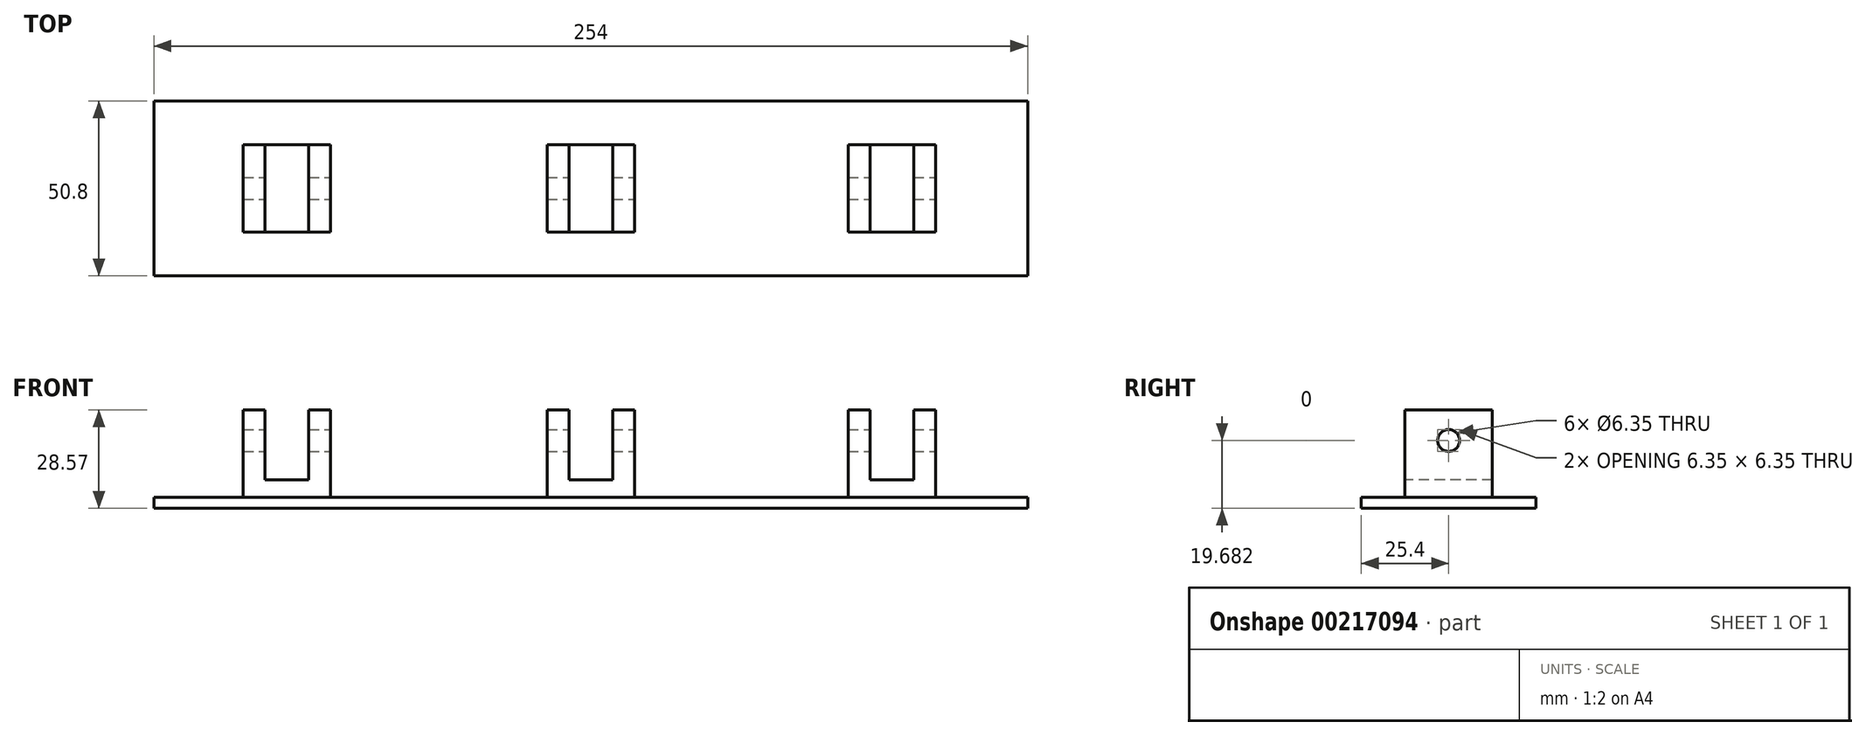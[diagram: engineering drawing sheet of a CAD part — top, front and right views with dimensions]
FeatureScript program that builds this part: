
annotation { "Feature Type Name" : "Feature", "Feature Type Description" : "" }
export const myFeature = defineFeature(function(context is Context, id is Id, definition is map)
    precondition{}
    {
        {
            var Q0;
            Q0=qCreatedBy(makeId("Top.planeOp"),FACE);
            var sketch = newSketch(context, id + "F0", { "sketchPlane" : qUnion([Q0])});
            skLineSegment(sketch, "E0.bottom", {"start": v(127, -25.4) * mm, "end": v(-127, -25.4) * mm});
            skLineSegment(sketch, "E0.top", {"start": v(127, 25.4) * mm, "end": v(-127, 25.4) * mm});
            skLineSegment(sketch, "E0.left", {"start": v(127, -25.4) * mm, "end": v(127, 25.4) * mm});
            skLineSegment(sketch, "E0.right", {"start": v(-127, -25.4) * mm, "end": v(-127, 25.4) * mm});
            skPoint(sketch, "E0.middle", {"position": v(0, 0) * mm});
            skSolve(sketch);
        }
        {
            var Q0;
            Q0=makeQuery(id+"F0.imprint","IMPRINT",FACE,{"disambiguationData":[TD([[makeQuery(id+"F0.imprint","IMPRINT",EDGE,{"derivedFrom":sQuery(id+"F0.wireOp",EDGE,"E0.bottom")}),-1.0]])]});
            extrude(context, id + "F1", {"entities" : qUnion([Q0]), "depth" : 3.17 * mm});
        }
        {
            var Q0;
            Q0=makeQuery(id+"F1.opExtrude","CAP_FACE",FACE,{"disambiguationData":[OSD([sQuery(id+"F0.wireOp",EDGE,"E0.bottom"),sQuery(id+"F0.wireOp",EDGE,"E0.top"),sQuery(id+"F0.wireOp",EDGE,"E0.left"),sQuery(id+"F0.wireOp",EDGE,"E0.right")])],"isStart":false});
            var sketch = newSketch(context, id + "F2", { "sketchPlane" : qUnion([Q0])});
            skLineSegment(sketch, "E1.bottom", {"start": v(12.7, -12.7) * mm, "end": v(-12.7, -12.7) * mm});
            skLineSegment(sketch, "E1.top", {"start": v(12.7, 12.7) * mm, "end": v(-12.7, 12.7) * mm});
            skLineSegment(sketch, "E1.left", {"start": v(12.7, -12.7) * mm, "end": v(12.7, 12.7) * mm});
            skLineSegment(sketch, "E1.right", {"start": v(-12.7, -12.7) * mm, "end": v(-12.7, 12.7) * mm});
            skPoint(sketch, "E1.middle", {"position": v(0, 0) * mm});
            skLineSegment(sketch, "E2.bottom", {"start": v(-75.67, -12.7) * mm, "end": v(-101.07, -12.7) * mm});
            skLineSegment(sketch, "E2.top", {"start": v(-75.67, 12.7) * mm, "end": v(-101.07, 12.7) * mm});
            skLineSegment(sketch, "E2.left", {"start": v(-75.67, -12.7) * mm, "end": v(-75.67, 12.7) * mm});
            skLineSegment(sketch, "E2.right", {"start": v(-101.07, -12.7) * mm, "end": v(-101.07, 12.7) * mm});
            skPoint(sketch, "E2.middle", {"position": v(-88.37, 0) * mm});
            skLineSegment(sketch, "E3.bottom", {"start": v(100.19, -12.7) * mm, "end": v(74.79, -12.7) * mm});
            skLineSegment(sketch, "E3.top", {"start": v(100.19, 12.7) * mm, "end": v(74.79, 12.7) * mm});
            skLineSegment(sketch, "E3.left", {"start": v(100.19, -12.7) * mm, "end": v(100.19, 12.7) * mm});
            skLineSegment(sketch, "E3.right", {"start": v(74.79, -12.7) * mm, "end": v(74.79, 12.7) * mm});
            skPoint(sketch, "E3.middle", {"position": v(87.49, 0) * mm});
            skSolve(sketch);
        }
        {
            var Q0;
            Q0=makeQuery(id+"F2.imprint","IMPRINT",FACE,{"disambiguationData":[TD([[makeQuery(id+"F2.imprint","IMPRINT",EDGE,{"derivedFrom":sQuery(id+"F2.wireOp",EDGE,"E2.bottom")}),-1.0]])]});
            var Q1;
            Q1=makeQuery(id+"F2.imprint","IMPRINT",FACE,{"disambiguationData":[TD([[makeQuery(id+"F2.imprint","IMPRINT",EDGE,{"derivedFrom":sQuery(id+"F2.wireOp",EDGE,"E1.bottom")}),-1.0]])]});
            var Q2;
            Q2=makeQuery(id+"F2.imprint","IMPRINT",FACE,{"disambiguationData":[TD([[makeQuery(id+"F2.imprint","IMPRINT",EDGE,{"derivedFrom":sQuery(id+"F2.wireOp",EDGE,"E3.bottom")}),-1.0]])]});
            extrude(context, id + "F3", {"entities" : qUnion([Q0, Q1, Q2]), "operationType" : NewBodyOperationType.ADD, "depth" : 25.4 * mm});
        }
        {
            var Q0;
            Q0=makeQuery(id+"F3.opExtrude","SWEPT_FACE",FACE,{"disambiguationData":[OSD([sQuery(id+"F2.wireOp",EDGE,"E2.bottom")])]});
            var sketch = newSketch(context, id + "F4", { "sketchPlane" : qUnion([Q0])});
            skLineSegment(sketch, "E4.bottom", {"start": v(-82.02, 8.2) * mm, "end": v(-94.72, 8.2) * mm});
            skLineSegment(sketch, "E4.top", {"start": v(-82.02, 48.95) * mm, "end": v(-94.72, 48.95) * mm});
            skLineSegment(sketch, "E4.left", {"start": v(-82.02, 8.2) * mm, "end": v(-82.02, 48.95) * mm});
            skLineSegment(sketch, "E4.right", {"start": v(-94.72, 8.2) * mm, "end": v(-94.72, 48.95) * mm});
            skPoint(sketch, "E4.middle", {"position": v(-88.37, 28.58) * mm});
            skLineSegment(sketch, "E5.bottom", {"start": v(6.35, 8.2) * mm, "end": v(-6.35, 8.2) * mm});
            skLineSegment(sketch, "E5.top", {"start": v(6.35, 48.95) * mm, "end": v(-6.35, 48.95) * mm});
            skLineSegment(sketch, "E5.left", {"start": v(6.35, 8.2) * mm, "end": v(6.35, 48.95) * mm});
            skLineSegment(sketch, "E5.right", {"start": v(-6.35, 8.2) * mm, "end": v(-6.35, 48.95) * mm});
            skPoint(sketch, "E5.middle", {"position": v(0, 28.58) * mm});
            skSolve(sketch);
        }
        {
            var Q0;
            Q0=makeQuery(id+"F3.opExtrude","SWEPT_FACE",FACE,{"disambiguationData":[OSD([sQuery(id+"F2.wireOp",EDGE,"E3.bottom")])]});
            var sketch = newSketch(context, id + "F5", { "sketchPlane" : qUnion([Q0])});
            skLineSegment(sketch, "E6.bottom", {"start": v(93.84, 8.2) * mm, "end": v(81.14, 8.2) * mm});
            skLineSegment(sketch, "E6.top", {"start": v(93.84, 48.95) * mm, "end": v(81.14, 48.95) * mm});
            skLineSegment(sketch, "E6.left", {"start": v(93.84, 8.2) * mm, "end": v(93.84, 48.95) * mm});
            skLineSegment(sketch, "E6.right", {"start": v(81.14, 8.2) * mm, "end": v(81.14, 48.95) * mm});
            skPoint(sketch, "E6.middle", {"position": v(87.49, 28.58) * mm});
            skSolve(sketch);
        }
        {
            var Q0;
            {var subQ0=sQuery(id+"F4.wireOp",EDGE,"E4.top");Q0=makeQuery(id+"F4.imprint","IMPRINT",FACE,{"disambiguationData":[TD([[makeQuery(id+"F4.imprint","IMPRINT",EDGE,{"derivedFrom":subQ0}),1.0]])]});}
            var Q1;
            {var subQ0=sQuery(id+"F4.wireOp",EDGE,"E4.bottom");Q1=makeQuery(id+"F4.imprint","IMPRINT",FACE,{"disambiguationData":[TD([[makeQuery(id+"F4.imprint","IMPRINT",EDGE,{"derivedFrom":subQ0}),-1.0]])]});}
            var Q2;
            Q2=makeQuery(id+"F4.imprint","IMPRINT",FACE,{"disambiguationData":[TD([[makeQuery(id+"F4.imprint","IMPRINT",EDGE,{"derivedFrom":sQuery(id+"F4.wireOp",EDGE,"E5.bottom")}),-1.0]])]});
            var Q3;
            {var subQ0=sQuery(id+"F5.wireOp",EDGE,"E6.top");Q3=makeQuery(id+"F5.imprint","IMPRINT",FACE,{"disambiguationData":[TD([[makeQuery(id+"F5.imprint","IMPRINT",EDGE,{"derivedFrom":subQ0}),1.0]])]});}
            var Q4;
            {var subQ0=sQuery(id+"F5.wireOp",EDGE,"E6.bottom");Q4=makeQuery(id+"F5.imprint","IMPRINT",FACE,{"disambiguationData":[TD([[makeQuery(id+"F5.imprint","IMPRINT",EDGE,{"derivedFrom":subQ0}),-1.0]])]});}
            extrude(context, id + "F6", {"entities" : qUnion([Q0, Q1, Q2, Q3, Q4]), "operationType" : NewBodyOperationType.REMOVE, "oppositeDirection" : true, "depth" : 38.1 * mm});
        }
        {
            var Q0;
            Q0=makeQuery(id+"F3.opExtrude","SWEPT_FACE",FACE,{"disambiguationData":[OSD([sQuery(id+"F2.wireOp",EDGE,"E3.left")])]});
            var sketch = newSketch(context, id + "F7", { "sketchPlane" : qUnion([Q0])});
            skCircle(sketch, "E7", {"center": v(0, 19.68) * mm, "radius": 3.18 * mm});
            skSolve(sketch);
        }
        {
            var Q0;
            Q0=makeQuery(id+"F7.imprint","IMPRINT",FACE,{"disambiguationData":[TD([[makeQuery(id+"F7.imprint","IMPRINT",EDGE,{"derivedFrom":sQuery(id+"F7.wireOp",EDGE,"E7")}),1.0]])]});
            extrude(context, id + "F8", {"entities" : qUnion([Q0]), "operationType" : NewBodyOperationType.REMOVE, "endBound" : BoundingType.THROUGH_ALL, "oppositeDirection" : true, "depth" : 25.4 * mm});
        }
    });
